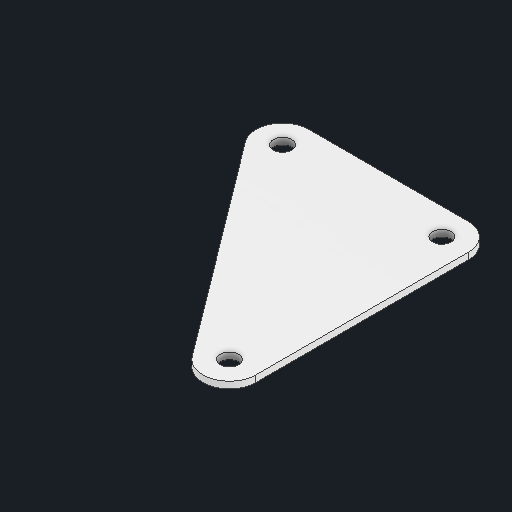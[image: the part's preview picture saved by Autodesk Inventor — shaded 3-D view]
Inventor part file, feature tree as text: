
AUTODESK INVENTOR PART (.ipt)
format: ipt  version: 2025 (Build 290162000, 162)  size: 99,328 bytes
history: native  units: in
note: dims shown in document units (in); Inventor stores cm internally (conversion verified against a paired STEP export)
features: other x3, extrude x1, sketch x1
ambient origin geometry x8: Origin, YZ Plane, XZ Plane, XY Plane, X Axis, Y Axis, Z Axis, Center Point
bodies: Solid1 (feature_tree)
feature tree (5):
  other  "Blocks"
  extrude  "Extrusion1"  Depth=0.0625in TaperAngle=0.0deg
  sketch  "Sketch1"  dims[d0=0.5in d1=0.5in d2=0.5in d3=0.0625in d4=0.0in]
  other  "main"
  other  "main:1"
